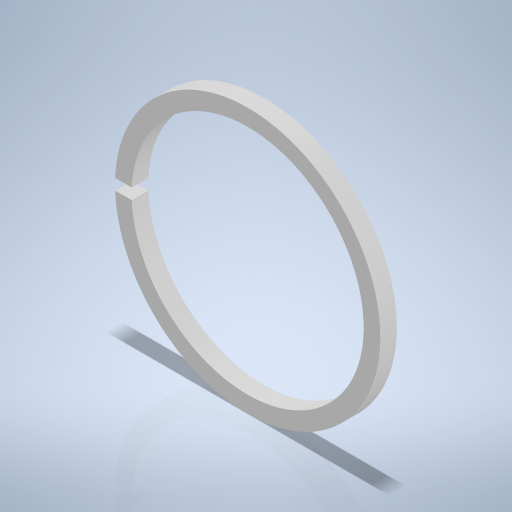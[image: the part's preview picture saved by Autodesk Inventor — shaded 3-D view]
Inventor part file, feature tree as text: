
AUTODESK INVENTOR PART (.ipt)
format: ipt  version: 2024 (Build 280153000, 153)  size: 256,000 bytes
history: native  units: mm
features: extrude x2, sketch x2
ambient origin geometry x8: Origin, YZ Plane, XZ Plane, XY Plane, X Axis, Y Axis, Z Axis, Center Point
bodies: Volumenkörper1 (feature_tree)
feature tree (4):
  extrude  "Extrusion1"  Depth=24.0mm
  extrude  "Extrusion2"  Depth=1.0mm
  sketch  "Skizze1"  dims[d0=21.0mm d1=24.0mm]
  sketch  "Skizze2"  dims[d2=1.5mm d3=0.0mm d4=1.0mm d5=1.5mm d6=0.0mm]
